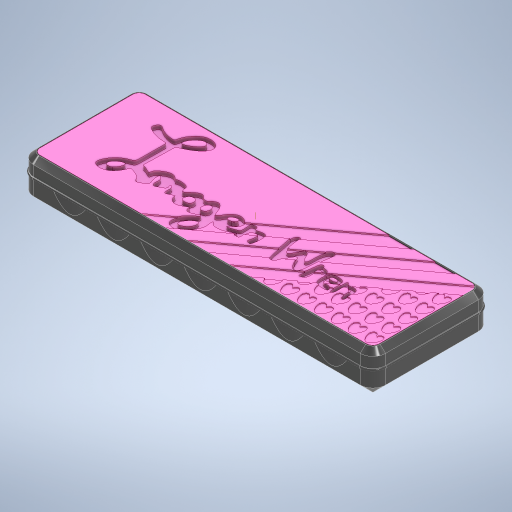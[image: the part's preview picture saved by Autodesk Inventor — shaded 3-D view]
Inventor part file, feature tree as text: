
AUTODESK INVENTOR PART (.ipt)
format: ipt  version: 2023 (Build 270158030, 158C)  size: 2,146,816 bytes
history: native  units: mm
features: projected_geometry x29, extrude x20, sketch x17, fillet x11, chamfer x5, other x4, pattern_circular x2, plane x1, pattern_linear x1, mirror x1
ambient origin geometry x8: Origin, YZ Plane, XZ Plane, XY Plane, X Axis, Y Axis, Z Axis, Center Point
bodies: Body1 (feature_tree), Body2 (feature_tree), Body3 (feature_tree)
feature tree (91):
  other  "case"
  extrude  "Extrusion1"  Depth=56.0mm
  extrude  "Extrusion2"  Depth=28.0mm
  extrude  "Extrusion3"  Depth=2.0mm
  fillet  "Fillet1"  Radius=4.0mm
  fillet  "Fillet2"  Radius=20.0mm
  fillet  "Fillet3"  Radius=4.0mm
  pattern_circular  "Circular Pattern1"  Count=2  [1 undecoded]
  fillet  "Fillet4"  Radius=96.0mm
  chamfer  "Chamfer1"  Distance=17.6mm
  extrude  "Extrusion4"  Depth=16.6mm
  chamfer  "Chamfer2"  Distance=20.0mm Angle=180.0deg
  extrude  "Extrusion5"  Depth=6.0mm TaperAngle=45.0deg
  pattern_circular  "Circular Pattern2"  [2 undecoded]
  fillet  "Fillet5"  Radius=5.0mm
  fillet  "Fillet6"  Radius=3.0mm
  fillet  "Fillet10"  Radius=6.0mm
  fillet  "Fillet11"  Radius=6.5mm
  fillet  "Fillet12"  Radius=6.5mm
  extrude  "Extrusion6"  Depth=22.0mm
  plane  "Work Plane1"
  extrude  "Extrusion7"  Depth=2.0mm TaperAngle=0.0deg
  extrude  "Extrusion8"  Depth=20.0mm TaperAngle=360.0deg
  extrude  "Extrusion9"  Depth=6.5mm
  fillet  "Fillet8"  Radius=6.5mm
  extrude  "Extrusion10"  Depth=2.0mm
  pattern_linear  "Rectangular Pattern1"  Spacing1=3.0mm  [1 undecoded]
  mirror  "Mirror1"
  extrude  "Extrusion11"  Depth=6.5mm
  extrude  "Extrusion15"  Depth=6.45mm
  extrude  "Extrusion16"  Depth=1.0mm
  chamfer  "Chamfer4"  Distance=3.0mm
  extrude  "Extrusion18"  Depth=3.1mm TaperAngle=0.0deg
  extrude  "Extrusion19"  Depth=1.8mm TaperAngle=0.0deg
  extrude  "Extrusion12"  Depth=0.5mm
  extrude  "Extrusion13"  Depth=1.0mm TaperAngle=0.0deg
  extrude  "Extrusion14"  Depth=0.5mm
  extrude  "Extrusion17"  Depth=60.0mm
  chamfer  "Chamfer5"  Distance=20.0mm
  chamfer  "Chamfer6"  Distance=29.0mm
  extrude  "Extrusion20"  Depth=8.5mm
  fillet  "Fillet13"  Radius=70.0mm
  sketch  "Sketch1"  dims[d0=167.0mm d1=56.0mm]
  sketch  "Sketch2"  dims[d2=83.5mm d3=28.0mm]
  projected_geometry  "Projected Loop1"
  sketch  "Sketch5"  dims[d4=18.0mm d5=0.0mm d6=2.0mm d8=4.0mm d9=20.0mm d10=4.0mm d11=20.0mm d12=96.0mm]
  projected_geometry  "Projected Loop5"
  sketch  "Sketch6"  dims[d13=65.0mm]
  other  "Work Axis1"
  sketch  "Sketch8"  dims[d14=74.2mm]
  projected_geometry  "Projected Loop7"
  other  "lid"
  sketch  "Sketch9"  dims[d15=12.0mm]
  projected_geometry  "Projected Loop8"
  sketch  "Sketch10"  dims[d16=14.3mm]
  projected_geometry  "Projected Loop9"
  sketch  "Sketch11"  dims[d17=12.4mm]
  projected_geometry  "Projected Loop10"
  sketch  "Sketch12"  dims[d18=0.95mm]
  projected_geometry  "Projected Loop11"
  sketch  "Sketch15"  dims[d19=0.95mm]
  sketch  "Sketch16"  dims[d20=2.0mm]
  other  "lid-part2"
  projected_geometry  "Projected Loop12"
  projected_geometry  "Projected Loop13"
  projected_geometry  "Projected Loop14"
  projected_geometry  "Projected Loop15"
  projected_geometry  "Projected Loop16"
  projected_geometry  "Projected Loop17"
  projected_geometry  "Projected Loop18"
  projected_geometry  "Projected Loop19"
  sketch  "Sketch18"  dims[d21=3.7mm d22=17.6mm d23=0.0mm]
  projected_geometry  "Projected Loop20"
  projected_geometry  "Projected Loop21"
  projected_geometry  "Projected Loop22"
  projected_geometry  "Projected Loop23"
  projected_geometry  "Projected Loop24"
  projected_geometry  "Projected Loop25"
  projected_geometry  "Projected Loop26"
  projected_geometry  "Projected Loop27"
  sketch  "Sketch19"  dims[d24=25.0mm d27=16.6mm d28=-1.745329mm]
  projected_geometry  "Projected Loop28"
  sketch  "Sketch20"  dims[d29=4.0mm]
  projected_geometry  "Projected Loop29"
  projected_geometry  "Projected Loop30"
  sketch  "Sketch21"  dims[d30=3.0mm]
  projected_geometry  "Projected Loop31"
  sketch  "Sketch22"  dims[d31=4.0mm d32=20.0mm d33=180.0deg]
  sketch  "Sketch23"  dims[d35=6.0mm d36=6.0mm d37=2.0mm d38=45.0deg d39=1.3mm d40=5.0mm d41=0.0mm d42=3.0mm d43=2.0mm d44=45.0deg d45=6.0mm d46=6.5mm d47=6.5mm d48=22.0mm d49=2.0mm d50=0.0mm d51=20.0mm d52=360.0deg d54=6.5mm d55=6.5mm d56=2.0mm d57=3.0mm d59=6.5mm d60=6.45mm d61=1.0mm d62=3.0mm d63=0.0mm d64=3.1mm d65=0.0mm d69=1.8mm d70=0.0mm d71=0.5mm d72=1.0mm d73=0.0mm d74=0.5mm d75=60.0mm d76=20.0mm d77=29.0mm d79=8.5mm d80=-1.745329mm d82=70.0mm d84=124.0mm d85=55.0mm d86=1.0mm d89=2.0mm d90=0.0mm d91=0.6mm d92=0.0mm d93=30.0deg d94=1.0mm d95=6.0mm d96=6.0mm d97=7.0mm d98=6.0mm d99=6.0mm d101=1.0mm d108=3.0mm d109=3.0mm d110=0.4mm d111=0.0mm d112=1.6mm d113=1.6mm d114=1.1mm d115=1.1mm d116=7.0mm d117=3.0mm d119=2.0mm d120=1.1mm d121=1.1mm d122=1.5mm d123=1.5mm d124=1.5mm d125=1.0mm d126=1.1mm d127=1.1mm d128=1.8mm d131=2.0mm d132=1.5mm d133=1.5mm d140=50.0mm d142=8.0mm d143=60.0mm d145=8.0mm d148=0.0mm d149=0.0mm d150=0.0mm d151=0.0mm d152=3.5mm d153=0.0mm d154=2.5mm d155=2.0mm d156=45.0deg d158=0.4mm d159=0.4mm d160=0.0mm d163=3.0mm d164=1.5mm d165=0.4mm d166=0.0mm d167=3.1mm d168=0.0mm d169=1.5mm d170=2.0mm d171=45.0deg d172=1.5mm d173=2.0mm d174=45.0deg d175=8.0mm d176=8.0mm d177=45.0mm d178=16.0mm d179=3.0mm d180=3.0mm d181=3.0mm d182=0.0mm d183=0.0mm d184=1.0mm]
  projected_geometry  "Projected Loop32"
  projected_geometry  "Projected Loop33"
note: 4 required parameter values undecoded (feature->parameter linkage not recoverable at this tier; creation-order binding heuristic only, values carry confidence <= 0.55)
